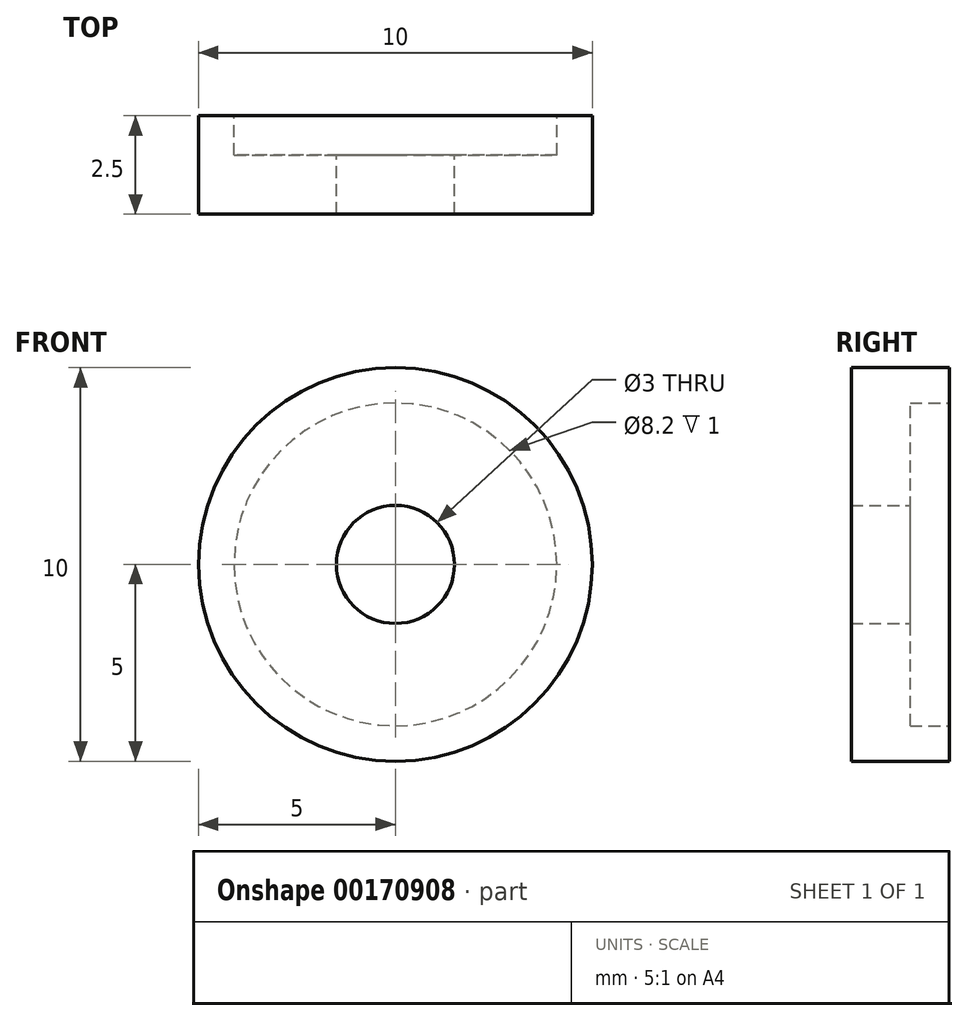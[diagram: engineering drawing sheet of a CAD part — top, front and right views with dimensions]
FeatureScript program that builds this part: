
annotation { "Feature Type Name" : "Feature", "Feature Type Description" : "" }
export const myFeature = defineFeature(function(context is Context, id is Id, definition is map)
    precondition{}
    {
        {
            var Q0;
            Q0=qCreatedBy(makeId("Front.planeOp"),FACE);
            var sketch = newSketch(context, id + "F0", { "sketchPlane" : qUnion([Q0])});
            skCircle(sketch, "E0", {"center": v(0, 0) * mm, "radius": 4.1 * mm});
            skCircle(sketch, "E1", {"center": v(0, 0) * mm, "radius": 1.5 * mm});
            skCircle(sketch, "E2", {"center": v(0, 0) * mm, "radius": 5 * mm});
            skSolve(sketch);
        }
        {
            var Q0;
            Q0=makeQuery(id+"F0.imprint","IMPRINT",FACE,{"disambiguationData":[TD([[makeQuery(id+"F0.imprint","IMPRINT",EDGE,{"derivedFrom":sQuery(id+"F0.wireOp",EDGE,"E0")}),-1.0]])]});
            var Q1;
            Q1=makeQuery(id+"F0.imprint","IMPRINT",FACE,{"disambiguationData":[TD([[makeQuery(id+"F0.imprint","IMPRINT",EDGE,{"derivedFrom":sQuery(id+"F0.wireOp",EDGE,"E0")}),1.0]])]});
            extrude(context, id + "F1", {"entities" : qUnion([Q0, Q1]), "offsetDistance" : 25 * mm, "depth" : 2.5 * mm});
        }
        {
            var Q0;
            Q0=makeQuery(id+"F0.imprint","IMPRINT",FACE,{"disambiguationData":[TD([[makeQuery(id+"F0.imprint","IMPRINT",EDGE,{"derivedFrom":sQuery(id+"F0.wireOp",EDGE,"E0")}),1.0]])]});
            extrude(context, id + "F2", {"entities" : qUnion([Q0]), "operationType" : NewBodyOperationType.REMOVE, "depth" : 1 * mm, "offsetDistance" : 25 * mm});
        }
    });
